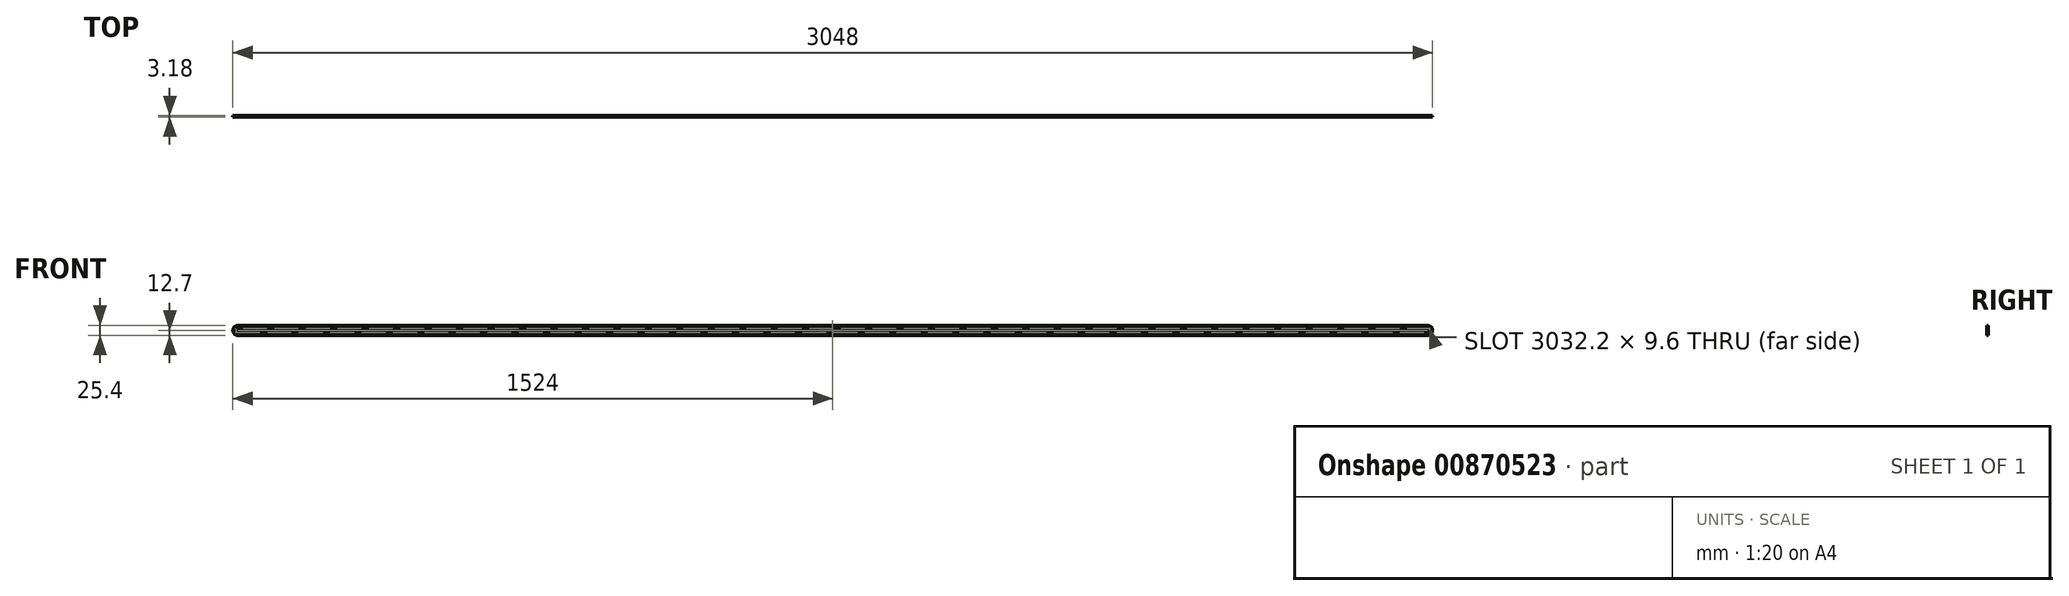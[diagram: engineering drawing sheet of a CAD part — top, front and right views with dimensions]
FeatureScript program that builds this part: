
annotation { "Feature Type Name" : "Feature", "Feature Type Description" : "" }
export const myFeature = defineFeature(function(context is Context, id is Id, definition is map)
    precondition{}
    {
        {
            var Q0;
            Q0=qCreatedBy(makeId("Front.planeOp"),FACE);
            var sketch = newSketch(context, id + "F0", { "sketchPlane" : qUnion([Q0])});
            skLineSegment(sketch, "E0.bottom", {"start": v(-682.83, 48.2) * mm, "end": v(2365.17, 48.2) * mm});
            skLineSegment(sketch, "E0.top", {"start": v(-682.83, 22.8) * mm, "end": v(2365.17, 22.8) * mm});
            skLineSegment(sketch, "E0.left", {"start": v(-682.83, 48.2) * mm, "end": v(-682.83, 22.8) * mm});
            skLineSegment(sketch, "E0.right", {"start": v(2365.17, 48.2) * mm, "end": v(2365.17, 22.8) * mm});
            skLineSegment(sketch, "E1", {"start": v(-682.83, 48.2) * mm, "end": v(2365.17, 22.8) * mm, "construction": true});
            skSolve(sketch);
        }
        {
            var Q0;
            Q0=makeQuery(id+"F0.imprint","IMPRINT",FACE,{"disambiguationData":[TD([[makeQuery(id+"F0.imprint","IMPRINT",EDGE,{"derivedFrom":sQuery(id+"F0.wireOp",EDGE,"E0.bottom")}),-1.0]])]});
            extrude(context, id + "F1", {"entities" : qUnion([Q0]), "depth" : 3.17 * mm, "offsetDistance" : 25.4 * mm});
        }
        {
            var Q0;
            Q0=makeQuery(id+"F1.opExtrude","SWEPT_EDGE",EDGE,{"disambiguationData":[OSD([sQuery(id+"F0.wireOp",EDGE,"E0.bottom"),sQuery(id+"F0.wireOp",EDGE,"E0.right")])]});
            var Q1;
            Q1=makeQuery(id+"F1.opExtrude","SWEPT_EDGE",EDGE,{"disambiguationData":[OSD([sQuery(id+"F0.wireOp",EDGE,"E0.top"),sQuery(id+"F0.wireOp",EDGE,"E0.right")])]});
            var Q2;
            Q2=makeQuery(id+"F1.opExtrude","SWEPT_EDGE",EDGE,{"disambiguationData":[OSD([sQuery(id+"F0.wireOp",EDGE,"E0.bottom"),sQuery(id+"F0.wireOp",EDGE,"E0.left")])]});
            var Q3;
            Q3=makeQuery(id+"F1.opExtrude","SWEPT_EDGE",EDGE,{"disambiguationData":[OSD([sQuery(id+"F0.wireOp",EDGE,"E0.top"),sQuery(id+"F0.wireOp",EDGE,"E0.left")])]});
            fillet(context, id + "F2", {"entities" : qUnion([Q0, Q1, Q2, Q3]), "radius" : 12.7 * mm, "tangentPropagation" : true, "allowEdgeOverflow" : false});
        }
        {
            var Q0;
            Q0=makeQuery(id+"F1.opExtrude","CAP_FACE",FACE,{"disambiguationData":[OSD([sQuery(id+"F0.wireOp",EDGE,"E0.bottom"),sQuery(id+"F0.wireOp",EDGE,"E0.top"),sQuery(id+"F0.wireOp",EDGE,"E0.left"),sQuery(id+"F0.wireOp",EDGE,"E0.right")])],"isStart":false});
            var sketch = newSketch(context, id + "F3", { "sketchPlane" : qUnion([Q0])});
            skCircle(sketch, "E2", {"center": v(-670.13, 35.5) * mm, "radius": 4.8 * mm});
            skCircle(sketch, "E3", {"center": v(2352.47, 35.5) * mm, "radius": 4.8 * mm});
            skSolve(sketch);
        }
        {
            var Q0;
            Q0=makeQuery(id+"F3.imprint","IMPRINT",FACE,{"disambiguationData":[TD([[makeQuery(id+"F3.imprint","IMPRINT",EDGE,{"derivedFrom":sQuery(id+"F3.wireOp",EDGE,"E2")}),1.0]])]});
            var Q1;
            Q1=makeQuery(id+"F3.imprint","IMPRINT",FACE,{"disambiguationData":[TD([[makeQuery(id+"F3.imprint","IMPRINT",EDGE,{"derivedFrom":sQuery(id+"F3.wireOp",EDGE,"E3")}),1.0]])]});
            var Q2;
            Q2=sQuery(id+"F3.wireOp",EDGE,"E2");
            extrude(context, id + "F4", {"entities" : qUnion([Q0, Q1]), "operationType" : NewBodyOperationType.REMOVE, "surfaceEntities" : qUnion([Q2]), "oppositeDirection" : true, "depth" : 3.17 * mm, "offsetDistance" : 25.4 * mm});
        }
        {
            var Q0;
            Q0=makeQuery(id+"F3.imprint","IMPRINT",FACE,{"disambiguationData":[TD([[makeQuery(id+"F3.imprint","IMPRINT",EDGE,{"derivedFrom":sQuery(id+"F3.wireOp",EDGE,"E2")}),-1.0]])]});
            var sketch = newSketch(context, id + "F5", { "sketchPlane" : qUnion([Q0])});
            skLineSegment(sketch, "E4", {"start": v(-670.13, 40.3) * mm, "end": v(2352.47, 40.3) * mm});
            skLineSegment(sketch, "E5", {"start": v(2352.47, 40.3) * mm, "end": v(2352.47, 30.7) * mm});
            skLineSegment(sketch, "E6", {"start": v(-670.13, 40.3) * mm, "end": v(-670.13, 30.7) * mm});
            skLineSegment(sketch, "E7", {"start": v(-670.13, 30.7) * mm, "end": v(2352.47, 30.7) * mm});
            skSolve(sketch);
        }
        {
            var Q0;
            Q0 = qSketchRegion(id + "F5", true);
            extrude(context, id + "F6", {"entities" : qUnion([Q0]), "operationType" : NewBodyOperationType.REMOVE, "oppositeDirection" : true, "depth" : 25.4 * mm, "offsetDistance" : 25.4 * mm});
        }
    });
